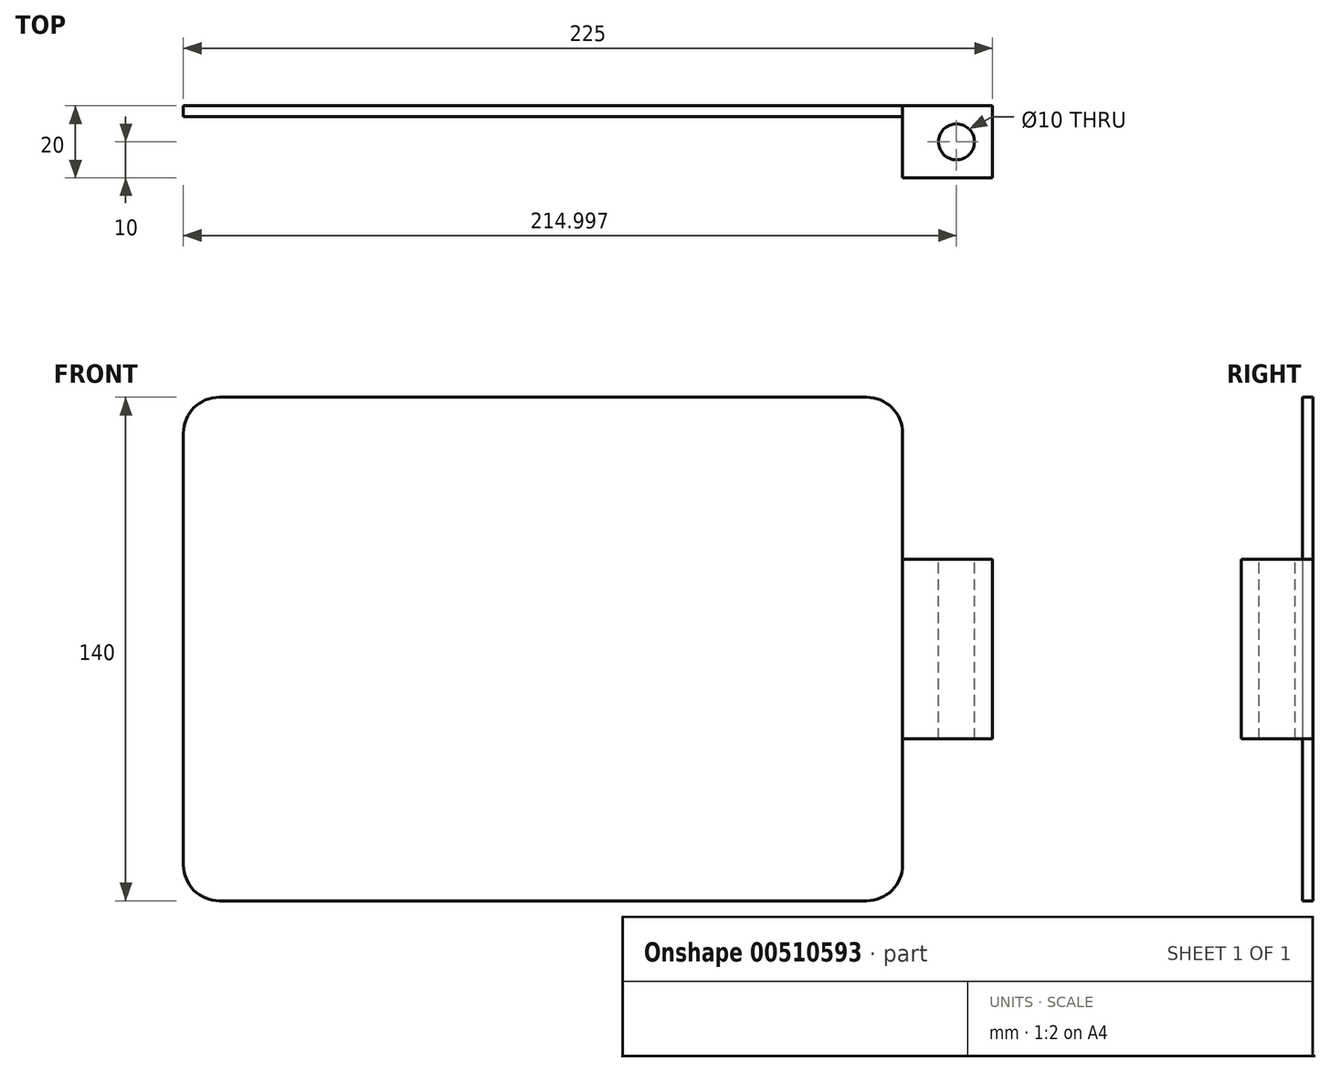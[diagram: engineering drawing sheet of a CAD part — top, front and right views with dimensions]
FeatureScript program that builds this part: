
annotation { "Feature Type Name" : "Feature", "Feature Type Description" : "" }
export const myFeature = defineFeature(function(context is Context, id is Id, definition is map)
    precondition{}
    {
        {
            var Q0;
            Q0=qCreatedBy(makeId("Front.planeOp"),FACE);
            var sketch = newSketch(context, id + "F0", { "sketchPlane" : qUnion([Q0])});
            skLineSegment(sketch, "E0.bottom", {"start": v(-83.28, 63.47) * mm, "end": v(116.72, 63.47) * mm});
            skLineSegment(sketch, "E0.top", {"start": v(-83.28, -76.53) * mm, "end": v(116.72, -76.53) * mm});
            skLineSegment(sketch, "E0.left", {"start": v(-83.28, 63.47) * mm, "end": v(-83.28, -76.53) * mm});
            skLineSegment(sketch, "E0.right", {"start": v(116.72, 63.47) * mm, "end": v(116.72, -76.53) * mm});
            skSolve(sketch);
        }
        {
            var Q0;
            Q0=makeQuery(id+"F0.imprint","IMPRINT",FACE,{"disambiguationData":[TD([[makeQuery(id+"F0.imprint","IMPRINT",EDGE,{"derivedFrom":sQuery(id+"F0.wireOp",EDGE,"E0.bottom")}),-1.0]])]});
            extrude(context, id + "F1", {"entities" : qUnion([Q0]), "depth" : 3 * mm});
        }
        {
            var Q0;
            Q0=makeQuery(id+"F1.opExtrude","SWEPT_EDGE",EDGE,{"disambiguationData":[OSD([sQuery(id+"F0.wireOp",EDGE,"E0.top"),sQuery(id+"F0.wireOp",EDGE,"E0.left")])]});
            var Q1;
            Q1=makeQuery(id+"F1.opExtrude","SWEPT_EDGE",EDGE,{"disambiguationData":[OSD([sQuery(id+"F0.wireOp",EDGE,"E0.bottom"),sQuery(id+"F0.wireOp",EDGE,"E0.right")])]});
            var Q2;
            Q2=makeQuery(id+"F1.opExtrude","SWEPT_EDGE",EDGE,{"disambiguationData":[OSD([sQuery(id+"F0.wireOp",EDGE,"E0.top"),sQuery(id+"F0.wireOp",EDGE,"E0.right")])]});
            var Q3;
            Q3=makeQuery(id+"F1.opExtrude","SWEPT_EDGE",EDGE,{"disambiguationData":[OSD([sQuery(id+"F0.wireOp",EDGE,"E0.bottom"),sQuery(id+"F0.wireOp",EDGE,"E0.left")])]});
            fillet(context, id + "F2", {"entities" : qUnion([Q0, Q1, Q2, Q3]), "radius" : 10 * mm, "tangentPropagation" : true, "allowEdgeOverflow" : false});
        }
        {
            var Q0;
            Q0=qCreatedBy(makeId("Front.planeOp"),FACE);
            var sketch = newSketch(context, id + "F3", { "sketchPlane" : qUnion([Q0])});
            skLineSegment(sketch, "E1.bottom", {"start": v(116.72, -31.53) * mm, "end": v(141.72, -31.53) * mm});
            skLineSegment(sketch, "E1.top", {"start": v(116.72, 18.47) * mm, "end": v(141.72, 18.47) * mm});
            skLineSegment(sketch, "E1.left", {"start": v(116.72, -31.53) * mm, "end": v(116.72, 18.47) * mm});
            skLineSegment(sketch, "E1.right", {"start": v(141.72, -31.53) * mm, "end": v(141.72, 18.47) * mm});
            skPoint(sketch, "E1.middle", {"position": v(129.22, -6.53) * mm});
            skSolve(sketch);
        }
        {
            var Q0;
            Q0=makeQuery(id+"F3.imprint","IMPRINT",FACE,{"disambiguationData":[TD([[makeQuery(id+"F3.imprint","IMPRINT",EDGE,{"derivedFrom":sQuery(id+"F3.wireOp",EDGE,"E1.bottom")}),1.0]])]});
            extrude(context, id + "F4", {"entities" : qUnion([Q0]), "operationType" : NewBodyOperationType.ADD, "depth" : 20 * mm});
        }
        {
            var Q0;
            Q0=makeQuery(id+"F4.opExtrude","SWEPT_FACE",FACE,{"disambiguationData":[OSD([sQuery(id+"F3.wireOp",EDGE,"E1.top")])]});
            var sketch = newSketch(context, id + "F5", { "sketchPlane" : qUnion([Q0])});
            skCircle(sketch, "E2", {"center": v(131.72, -10) * mm, "radius": 5 * mm});
            skSolve(sketch);
        }
        {
            var Q0;
            Q0=makeQuery(id+"F5.imprint","IMPRINT",FACE,{"disambiguationData":[TD([[makeQuery(id+"F5.imprint","IMPRINT",EDGE,{"derivedFrom":sQuery(id+"F5.wireOp",EDGE,"E2")}),1.0]])]});
            extrude(context, id + "F6", {"entities" : qUnion([Q0]), "operationType" : NewBodyOperationType.REMOVE, "oppositeDirection" : true, "depth" : 87.53 * mm});
        }
    });
